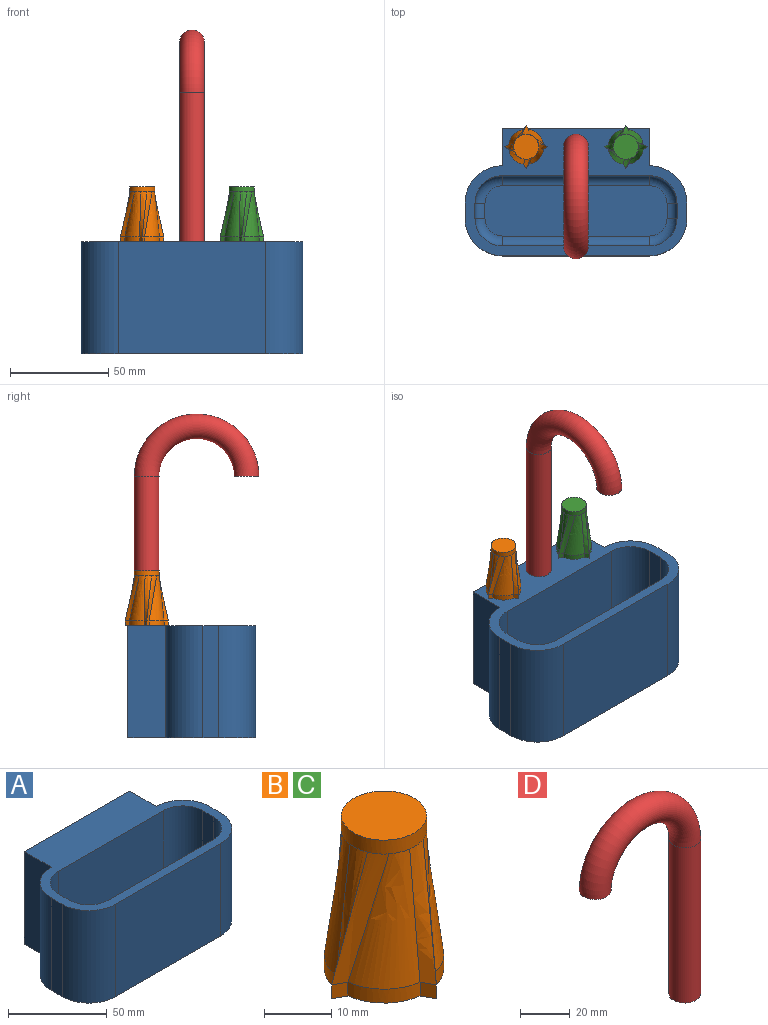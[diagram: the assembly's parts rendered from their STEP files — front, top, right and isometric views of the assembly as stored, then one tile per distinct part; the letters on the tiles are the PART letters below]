
ASSEMBLY  parts=4 mates=3
PART A: 29 faces, bbox 113.1x65.1x57.2 mm
  f0: cylinder r=13.97mm len=45.72mm, axis (0,0,1), area 1003.3mm2, adj f1,f17,f18,f27
  f1: plane 45.72x7.8mm, normal (1,0,0), area 356.8mm2, adj f0,f2,f18,f25
  f2: cylinder r=13.97mm len=45.72mm, axis (0,0,1), area 1003.3mm2, adj f1,f3,f18,f23
  f3: plane 75.02x45.72mm, normal (0,-1,0), area 3429.8mm2, adj f2,f4,f18,f21
  f4: cylinder r=13.97mm len=45.72mm, axis (0,0,1), area 1003.3mm2, adj f3,f5,f18,f22
  f5: plane 45.72x7.8mm, normal (-1,0,0), area 356.8mm2, adj f4,f6,f18,f24
  f6: cylinder r=13.97mm len=45.72mm, axis (0,0,1), area 1003.3mm2, adj f5,f17,f18,f26
  f7: plane 75.02x57.15mm, normal (0,1,0), area 4287.3mm2, adj f8,f16,f18,f20
  f8: plane 57.15x19.21mm, normal (-1,0,0), area 1097.9mm2, adj f7,f9,f18,f20
  f9: cylinder r=19.05mm len=57.15mm, axis (0,0,1), area 1710.1mm2, adj f8,f10,f18,f20
  f10: plane 57.15x7.8mm, normal (-1,0,0), area 446mm2, adj f9,f11,f18,f20
  f11: cylinder r=19.05mm len=57.15mm, axis (0,0,1), area 1710.1mm2, adj f10,f12,f18,f20
  f12: plane 75.02x57.15mm, normal (0,-1,0), area 4287.3mm2, adj f11,f13,f18,f20
  f13: cylinder r=19.05mm len=57.15mm, axis (0,0,1), area 1710.1mm2, adj f12,f14,f18,f20
  f14: plane 57.15x7.8mm, normal (1,0,0), area 446mm2, adj f13,f15,f18,f20
  f15: cylinder r=19.05mm len=57.15mm, axis (0,0,1), area 1710.1mm2, adj f14,f16,f18,f20
  f16: plane 57.15x19.21mm, normal (1,0,0), area 1097.9mm2, adj f7,f15,f18,f20
  f17: plane 75.02x45.72mm, normal (0,1,0), area 3429.8mm2, adj f0,f6,f18,f28
  f18: plane 113.12x65.11mm, normal (0,0,1), area 2809.6mm2, adj f0,f1,f2,f3,f4,f5,f6,f7
  f19: plane 92.8x25.58mm, normal (0,0,1), area 2306.2mm2, adj f21,f22,f23,f24,f25,f26,f27,f28
  f20: plane 113.12x65.11mm, normal (0,0,-1), area 6322.1mm2, adj f7,f8,f9,f10,f11,f12,f13,f14
  f21: cylinder r=5.08mm len=75.02mm, axis (1,0,0), area 598.6mm2, adj f3,f19,f22,f23
  f22: torus R=8.89mm, axis (0,0,-1), area 152mm2, adj f4,f19,f21,f24
  f23: torus R=8.89mm, axis (0,0,-1), area 152mm2, adj f2,f19,f21,f25
  f24: cylinder r=5.08mm len=7.8mm, axis (0,-1,0), area 62.3mm2, adj f5,f19,f22,f26
  f25: cylinder r=5.08mm len=7.8mm, axis (0,1,0), area 62.3mm2, adj f1,f19,f23,f27
  f26: torus R=8.89mm, axis (0,0,-1), area 152mm2, adj f6,f19,f24,f28
  f27: torus R=8.89mm, axis (0,0,-1), area 152mm2, adj f0,f19,f25,f28
  f28: cylinder r=5.08mm len=75.02mm, axis (-1,0,0), area 598.6mm2, adj f17,f19,f26,f27
PART B: 27 faces, bbox 22.1x22.1x27.9 mm
  f0: cylinder r=8.89mm len=7.59mm, axis (0,0,-1), area 29.3mm2, adj f1,f11,f12,f17
  f1: plane 2.54x2.23mm, normal (-0.48,0.88,0), area 6.5mm2, adj f0,f2,f12,f18
  f2: plane 2.54x2.23mm, normal (-0.48,-0.88,0), area 6.5mm2, adj f1,f3,f12,f19
  f3: cylinder r=8.89mm len=7.59mm, axis (0,0,-1), area 29.3mm2, adj f2,f4,f12,f20
  f4: plane 2.54x2.23mm, normal (-0.88,-0.48,0), area 6.5mm2, adj f3,f5,f12,f21
  f5: plane 2.54x2.23mm, normal (0.88,-0.48,0), area 6.5mm2, adj f4,f6,f12,f22
  f6: cylinder r=8.89mm len=7.59mm, axis (0,0,-1), area 29.3mm2, adj f5,f7,f12,f23
  f7: plane 2.54x2.23mm, normal (0.48,-0.88,0), area 6.5mm2, adj f6,f8,f12,f24
  f8: plane 2.54x2.23mm, normal (0.48,0.88,0), area 6.5mm2, adj f7,f9,f12,f25
  f9: cylinder r=8.89mm len=7.59mm, axis (0,0,-1), area 29.3mm2, adj f8,f10,f12,f26
  f10: plane 2.54x2.23mm, normal (0.88,0.48,0), area 6.5mm2, adj f9,f11,f12,f15
  f11: plane 2.54x2.23mm, normal (-0.88,0.48,0), area 6.5mm2, adj f0,f10,f12,f16
  f12: plane 22.07x22.07mm, normal (0,0,-1), area 258.6mm2, adj f0,f1,f2,f3,f4,f5,f6,f7
  f13: cylinder r=6.35mm len=12.7mm, axis (0,0,-1), area 101.3mm2, adj f14,f15,f16,f17,f18,f19,f20,f21
  f14: plane 12.7x12.7mm, normal (0,0,1), area 126.7mm2, adj f13
  f15: bspline ~22.86x5.15mm, area 60.2mm2, adj f10,f13,f16,f26
  f16: bspline ~22.86x7.14mm, area 66.1mm2, adj f11,f13,f15,f17
  f17: bspline ~22.86x7.94mm, area 169mm2, adj f0,f13,f16,f18
  f18: bspline ~22.86x5.15mm, area 60.2mm2, adj f1,f13,f17,f19
  f19: bspline ~22.86x7.14mm, area 66.1mm2, adj f2,f13,f18,f20
  f20: bspline ~22.86x7.94mm, area 169mm2, adj f3,f13,f19,f21
  f21: bspline ~22.86x5.15mm, area 60.2mm2, adj f4,f13,f20,f22
  f22: bspline ~22.86x7.14mm, area 66.1mm2, adj f5,f13,f21,f23
  f23: bspline ~22.86x7.94mm, area 169mm2, adj f6,f13,f22,f24
  f24: bspline ~22.86x5.15mm, area 60.2mm2, adj f7,f13,f23,f25
  f25: bspline ~22.86x7.14mm, area 66.1mm2, adj f8,f13,f24,f26
  f26: bspline ~22.86x7.94mm, area 169mm2, adj f9,f13,f15,f25
PART C: same geometry as B
PART D: 4 faces, bbox 68.7x12.7x110.6 mm
  f0: plane 12.7x12.7mm, normal (0,0,-1), area 126.7mm2, adj f2
  f1: plane 12.7x12.7mm, normal (0,0,-1), area 126.7mm2, adj f3
  f2: cylinder r=6.35mm len=76.2mm, axis (0,0,1), area 3040.2mm2, adj f0,f3
  f3: torus R=25.4mm, axis (0,-1,0), area 3183.7mm2, adj f1,f2
PLACE A t=(-4.41,-79.74,5.11)mm
PLACE B t=(-29.81,-47.19,5.11)mm
PLACE C t=(20.99,-47.19,5.11)mm
PLACE D rot(axis=(0,0,1),90deg) t=(-4.41,-47.19,5.11)mm
MATE revolute C.f0 <-> A.f18  axis (0,0,-1) through (20.99,-47.19,5.11)mm
MATE revolute B.f0 <-> A.f18  axis (0,0,-1) through (-29.81,-47.19,5.11)mm
MATE revolute D.f2 <-> A.f18  axis (0,0,-1) through (-4.41,-47.19,5.11)mm
